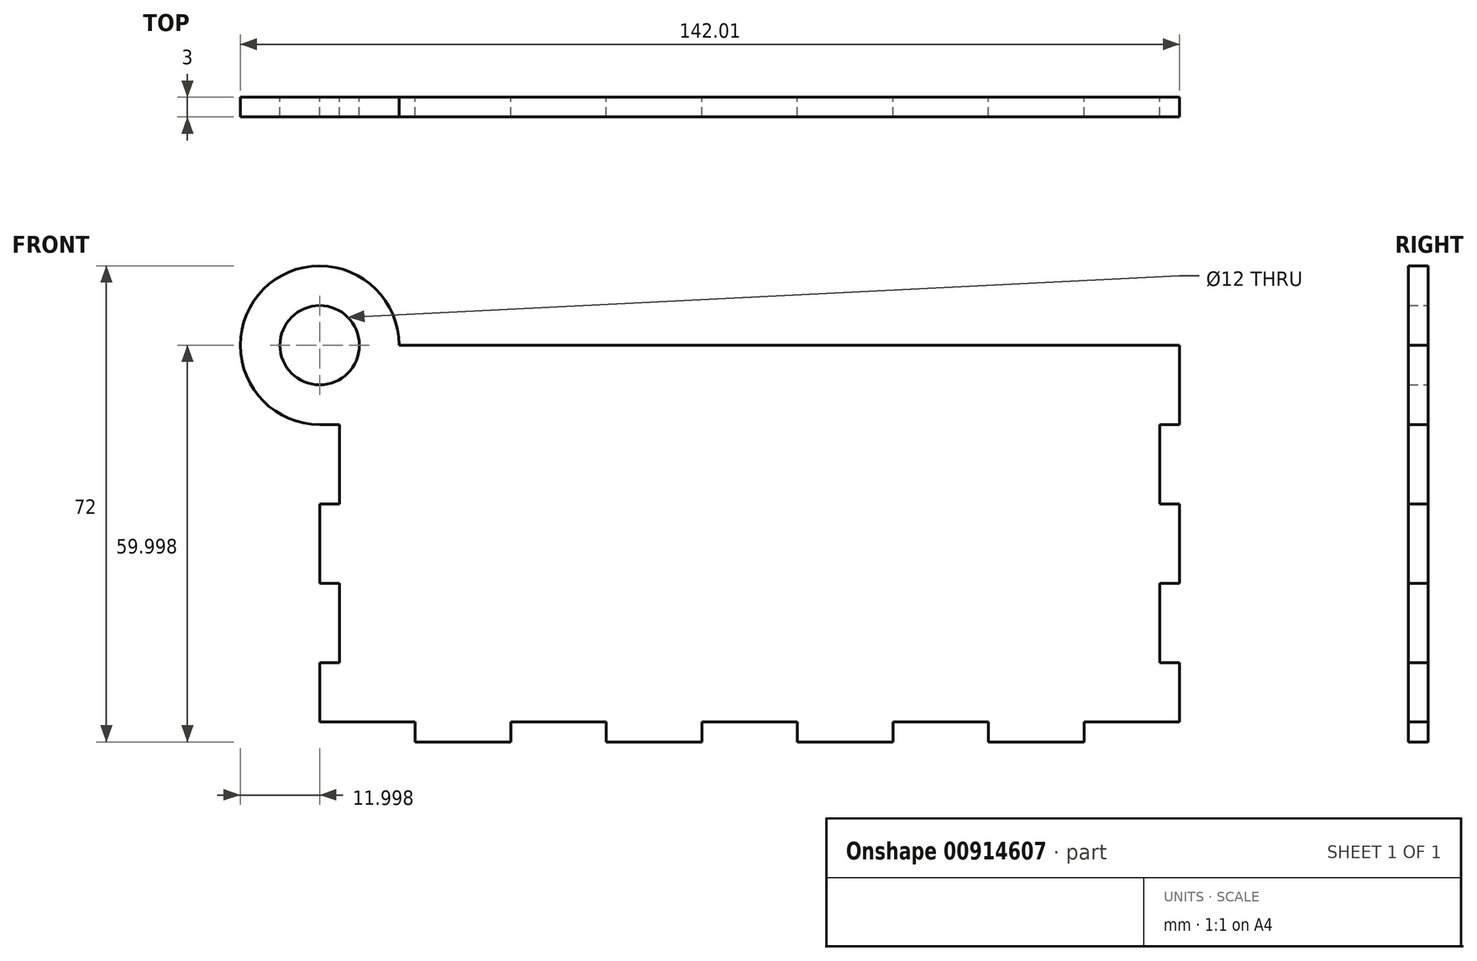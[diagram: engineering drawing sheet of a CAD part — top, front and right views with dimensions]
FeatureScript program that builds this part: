
annotation { "Feature Type Name" : "Feature", "Feature Type Description" : "" }
export const myFeature = defineFeature(function(context is Context, id is Id, definition is map)
    precondition{}
    {
        {
            var Q0;
            Q0=qCreatedBy(makeId("Front.planeOp"),FACE);
            var sketch = newSketch(context, id + "F0", { "sketchPlane" : qUnion([Q0])});
            skLineSegment(sketch, "E0", {"start": v(40.16, 28.16) * mm, "end": v(43.16, 28.16) * mm});
            skLineSegment(sketch, "E1", {"start": v(40.16, 16.16) * mm, "end": v(43.16, 16.16) * mm});
            skLineSegment(sketch, "E2", {"start": v(40.16, 4.16) * mm, "end": v(43.16, 4.16) * mm});
            skLineSegment(sketch, "E3", {"start": v(40.16, -7.84) * mm, "end": v(43.16, -7.84) * mm});
            skPoint(sketch, "E4.orphan", {"position": v(43.16, -19.84) * mm});
            skLineSegment(sketch, "E5.MirrorCS", {"start": v(-83.85, 40.16) * mm, "end": v(-83.84, 40.16) * mm});
            skLineSegment(sketch, "E6.MirrorCS", {"start": v(-86.84, 40.15) * mm, "end": v(-83.84, 40.15) * mm});
            skLineSegment(sketch, "E7.MirrorCS", {"start": v(-83.85, 40.16) * mm, "end": v(-83.85, 40.15) * mm});
            skLineSegment(sketch, "E8.MirrorCS", {"start": v(-83.84, 40.15) * mm, "end": v(-83.84, 43.15) * mm});
            skLineSegment(sketch, "E9.MirrorCS", {"start": v(-83.84, 43.15) * mm, "end": v(-86.84, 43.15) * mm});
            skLineSegment(sketch, "E10.MirrorCS", {"start": v(-83.85, 16.16) * mm, "end": v(-86.85, 16.16) * mm});
            skLineSegment(sketch, "E11.MirrorCS", {"start": v(-86.84, 43.15) * mm, "end": v(-86.84, 40.15) * mm});
            skLineSegment(sketch, "E12.MirrorCS", {"start": v(-83.85, 28.16) * mm, "end": v(-86.85, 28.16) * mm});
            skLineSegment(sketch, "E13.MirrorCS", {"start": v(-83.85, -7.84) * mm, "end": v(-86.85, -7.84) * mm});
            skLineSegment(sketch, "E14.MirrorCS", {"start": v(-83.85, 4.16) * mm, "end": v(-86.85, 4.16) * mm});
            skArc(sketch, "E15.MirrorCS", {"start": v(-86.85, 28.16) * mm, "mid": v(-95.34, 48.64) * mm, "end": v(-74.85, 40.16) * mm});
            skPoint(sketch, "E16.MirrorP", {"position": v(-86.84, -19.84) * mm});
            skCircle(sketch, "E17.MirrorC", {"center": v(-86.85, 40.16) * mm, "radius": 6 * mm});
            skLineSegment(sketch, "E18.trimOffspring", {"start": v(-83.84, 40.16) * mm, "end": v(-86.85, 40.16) * mm});
            skLineSegment(sketch, "E19", {"start": v(-83.85, -16.84) * mm, "end": v(-72.4, -16.84) * mm});
            skLineSegment(sketch, "E20", {"start": v(-72.4, -16.84) * mm, "end": v(-72.4, -19.84) * mm});
            skLineSegment(sketch, "E21", {"start": v(-57.96, -16.84) * mm, "end": v(-57.96, -19.84) * mm});
            skLineSegment(sketch, "E22", {"start": v(-43.51, -16.84) * mm, "end": v(-43.51, -19.84) * mm});
            skLineSegment(sketch, "E23", {"start": v(-29.07, -16.84) * mm, "end": v(-29.07, -19.84) * mm});
            skLineSegment(sketch, "E24", {"start": v(-14.62, -16.84) * mm, "end": v(-14.62, -19.84) * mm});
            skLineSegment(sketch, "E25", {"start": v(-0.18, -16.84) * mm, "end": v(-0.18, -19.84) * mm});
            skLineSegment(sketch, "E26", {"start": v(14.27, -16.84) * mm, "end": v(14.27, -19.84) * mm});
            skLineSegment(sketch, "E27", {"start": v(28.71, -16.84) * mm, "end": v(28.71, -19.84) * mm});
            skLineSegment(sketch, "E28.trimOffspring", {"start": v(-86.84, -19.84) * mm, "end": v(-86.85, -19.84) * mm});
            skLineSegment(sketch, "E29.trimOffspring", {"start": v(-57.96, -16.84) * mm, "end": v(-43.51, -16.84) * mm});
            skLineSegment(sketch, "E30.trimOffspring", {"start": v(-57.96, -19.84) * mm, "end": v(-72.4, -19.84) * mm});
            skLineSegment(sketch, "E31.trimOffspring", {"start": v(-29.07, -16.84) * mm, "end": v(-14.62, -16.84) * mm});
            skLineSegment(sketch, "E32.trimOffspring", {"start": v(-29.07, -19.84) * mm, "end": v(-43.51, -19.84) * mm});
            skLineSegment(sketch, "E33.trimOffspring", {"start": v(-0.18, -16.84) * mm, "end": v(14.27, -16.84) * mm});
            skLineSegment(sketch, "E34.trimOffspring", {"start": v(-0.18, -19.84) * mm, "end": v(-14.62, -19.84) * mm});
            skLineSegment(sketch, "E35.trimOffspring", {"start": v(28.71, -16.84) * mm, "end": v(40.16, -16.84) * mm});
            skLineSegment(sketch, "E36.trimOffspring", {"start": v(28.71, -19.84) * mm, "end": v(14.27, -19.84) * mm});
            skPoint(sketch, "E37.start.orphan", {"position": v(86.48, -16.84) * mm});
            skPoint(sketch, "E38.end.orphan", {"position": v(57.6, -19.84) * mm});
            skLineSegment(sketch, "E39", {"start": v(-74.85, 40.16) * mm, "end": v(40.16, 40.16) * mm});
            skLineSegment(sketch, "E40", {"start": v(-86.85, 16.16) * mm, "end": v(-86.85, 4.16) * mm});
            skLineSegment(sketch, "E41", {"start": v(-86.85, -7.84) * mm, "end": v(-86.85, -16.84) * mm});
            skLineSegment(sketch, "E42", {"start": v(-86.85, -16.84) * mm, "end": v(-83.85, -16.84) * mm});
            skLineSegment(sketch, "E43", {"start": v(-83.85, 28.16) * mm, "end": v(-83.85, 16.16) * mm});
            skLineSegment(sketch, "E44", {"start": v(-83.85, 4.16) * mm, "end": v(-83.85, -7.84) * mm});
            skPoint(sketch, "E45.MirrorCS.end.orphan", {"position": v(-86.85, 28.16) * mm});
            skLineSegment(sketch, "E46", {"start": v(43.16, 28.16) * mm, "end": v(43.16, 40.16) * mm});
            skLineSegment(sketch, "E47", {"start": v(43.16, 40.16) * mm, "end": v(40.16, 40.16) * mm});
            skLineSegment(sketch, "E48", {"start": v(40.16, 28.16) * mm, "end": v(40.16, 16.16) * mm});
            skLineSegment(sketch, "E49", {"start": v(43.16, 16.16) * mm, "end": v(43.16, 4.16) * mm});
            skLineSegment(sketch, "E50", {"start": v(40.16, 4.16) * mm, "end": v(40.16, -7.84) * mm});
            skLineSegment(sketch, "E51", {"start": v(43.16, -7.84) * mm, "end": v(43.16, -16.84) * mm});
            skLineSegment(sketch, "E52", {"start": v(43.16, -16.84) * mm, "end": v(40.16, -16.84) * mm});
            skSolve(sketch);
        }
        {
            var Q0;
            Q0=makeQuery(id+"F0.imprint","IMPRINT",FACE,{"disambiguationData":[TD([[makeQuery(id+"F0.imprint","IMPRINT",EDGE,{"derivedFrom":sQuery(id+"F0.wireOp",EDGE,"E0")}),1.0]])]});
            extrude(context, id + "F1", {"entities" : qUnion([Q0]), "depth" : 3 * mm, "offsetDistance" : 25 * mm});
        }
    });
